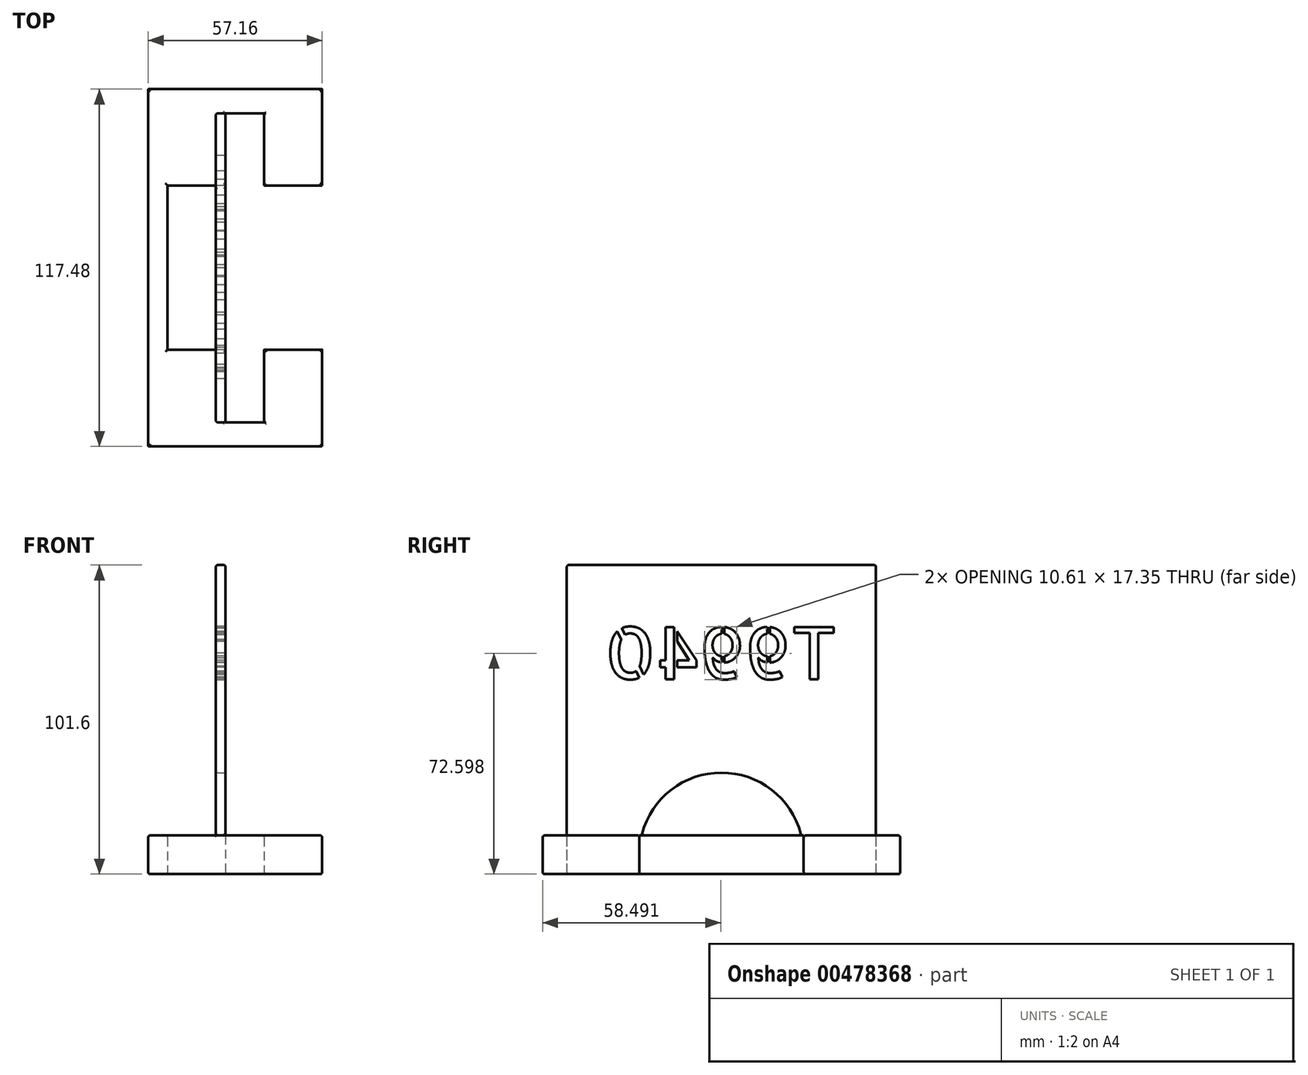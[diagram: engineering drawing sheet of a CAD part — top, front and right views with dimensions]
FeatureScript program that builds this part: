
annotation { "Feature Type Name" : "Feature", "Feature Type Description" : "" }
export const myFeature = defineFeature(function(context is Context, id is Id, definition is map)
    precondition{}
    {
        {
            var Q0;
            Q0=qCreatedBy(makeId("Top.planeOp"),FACE);
            var sketch = newSketch(context, id + "F0", { "sketchPlane" : qUnion([Q0])});
            skLineSegment(sketch, "E0.bottom", {"start": v(28.58, 58.74) * mm, "end": v(-28.57, 58.74) * mm});
            skLineSegment(sketch, "E0.top", {"start": v(28.58, -58.74) * mm, "end": v(-28.57, -58.74) * mm});
            skLineSegment(sketch, "E0.left", {"start": v(28.58, 58.74) * mm, "end": v(28.58, 27.05) * mm});
            skLineSegment(sketch, "E0.right", {"start": v(-28.57, 58.74) * mm, "end": v(-28.57, -58.74) * mm});
            skPoint(sketch, "E0.middle", {"position": v(0, 0) * mm});
            skLineSegment(sketch, "E1.bottom", {"start": v(9.53, 50.8) * mm, "end": v(-3.17, 50.8) * mm});
            skLineSegment(sketch, "E1.top", {"start": v(9.53, -50.8) * mm, "end": v(-3.17, -50.8) * mm});
            skLineSegment(sketch, "E1.left", {"start": v(9.53, 50.8) * mm, "end": v(9.53, 27.05) * mm});
            skLineSegment(sketch, "E1.right", {"start": v(-3.17, 50.8) * mm, "end": v(-3.17, 27.05) * mm});
            skLineSegment(sketch, "E2.bottom", {"start": v(28.58, -26.92) * mm, "end": v(9.53, -26.92) * mm});
            skLineSegment(sketch, "E2.top", {"start": v(28.58, 27.05) * mm, "end": v(9.53, 27.05) * mm});
            skLineSegment(sketch, "E2.right", {"start": v(-22.22, -26.92) * mm, "end": v(-22.22, 27.05) * mm});
            skPoint(sketch, "E2.middle", {"position": v(3.18, 0.06) * mm});
            skLineSegment(sketch, "E3.trimOffspring", {"start": v(28.58, -26.92) * mm, "end": v(28.58, -58.74) * mm});
            skLineSegment(sketch, "E4.trimOffspring", {"start": v(9.53, -26.92) * mm, "end": v(9.53, -50.8) * mm});
            skLineSegment(sketch, "E5.trimOffspring", {"start": v(-3.17, -26.92) * mm, "end": v(-3.17, -50.8) * mm});
            skLineSegment(sketch, "E6.trimOffspring", {"start": v(-3.17, 27.05) * mm, "end": v(-22.22, 27.05) * mm});
            skLineSegment(sketch, "E7.trimOffspring", {"start": v(-3.17, -26.92) * mm, "end": v(-22.22, -26.92) * mm});
            skSolve(sketch);
        }
        {
            var Q0;
            Q0 = qSketchRegion(id + "F0", true);
            extrude(context, id + "F1", {"entities" : qUnion([Q0]), "depth" : 12.7 * mm});
        }
        {
            var Q0;
            Q0=makeQuery(id+"F1.opExtrude","CAP_FACE",FACE,{"disambiguationData":[OSD([sQuery(id+"F0.wireOp",EDGE,"E0.bottom"),sQuery(id+"F0.wireOp",EDGE,"E0.top"),sQuery(id+"F0.wireOp",EDGE,"E0.left"),sQuery(id+"F0.wireOp",EDGE,"E0.right"),sQuery(id+"F0.wireOp",EDGE,"E1.bottom"),sQuery(id+"F0.wireOp",EDGE,"E1.top"),sQuery(id+"F0.wireOp",EDGE,"E1.left"),sQuery(id+"F0.wireOp",EDGE,"E1.right"),sQuery(id+"F0.wireOp",EDGE,"E2.bottom"),sQuery(id+"F0.wireOp",EDGE,"E2.top"),sQuery(id+"F0.wireOp",EDGE,"E2.right"),sQuery(id+"F0.wireOp",EDGE,"E3.trimOffspring"),sQuery(id+"F0.wireOp",EDGE,"E4.trimOffspring"),sQuery(id+"F0.wireOp",EDGE,"E5.trimOffspring"),sQuery(id+"F0.wireOp",EDGE,"E6.trimOffspring"),sQuery(id+"F0.wireOp",EDGE,"E7.trimOffspring")])],"isStart":false});
            var sketch = newSketch(context, id + "F2", { "sketchPlane" : qUnion([Q0])});
            skLineSegment(sketch, "E8.bottom", {"start": v(-3.17, 50.8) * mm, "end": v(-6.35, 50.8) * mm});
            skLineSegment(sketch, "E8.top", {"start": v(-3.17, -50.8) * mm, "end": v(-6.35, -50.8) * mm});
            skLineSegment(sketch, "E8.left", {"start": v(-3.17, 50.8) * mm, "end": v(-3.17, -50.8) * mm});
            skLineSegment(sketch, "E8.right", {"start": v(-6.35, 50.8) * mm, "end": v(-6.35, -50.8) * mm});
            skSolve(sketch);
        }
        {
            var Q0;
            Q0 = qSketchRegion(id + "F2", true);
            extrude(context, id + "F3", {"entities" : qUnion([Q0]), "operationType" : NewBodyOperationType.ADD, "depth" : 88.9 * mm});
        }
        {
            var Q0;
            Q0=makeQuery(id+"F3.boolean.opBoolean","MERGE",FACE,{"derivedFrom":[makeQuery(id+"F1.opExtrude","SWEPT_FACE",FACE,{"disambiguationData":[OSD([sQuery(id+"F0.wireOp",EDGE,"E1.right")])]}),makeQuery(id+"F1.opExtrude","SWEPT_FACE",FACE,{"disambiguationData":[OSD([sQuery(id+"F0.wireOp",EDGE,"E5.trimOffspring")])]}),makeQuery(id+"F3.opExtrude","SWEPT_FACE",FACE,{"disambiguationData":[OSD([sQuery(id+"F2.wireOp",EDGE,"E8.left")])]})]});
            var sketch = newSketch(context, id + "F4", { "sketchPlane" : qUnion([Q0])});
            skCircle(sketch, "E9", {"center": v(0, 6.35) * mm, "radius": 26.99 * mm});
            skSolve(sketch);
        }
        {
            var Q0;
            {var subQ0=sQuery(id+"F4.wireOp",EDGE,"E9");var subQ1=makeQuery(id+"F3.opExtrude","CAP_EDGE",EDGE,{"disambiguationData":[OSD([sQuery(id+"F2.wireOp",EDGE,"E8.left")])],"isStart":true});var subQ2=makeQuery(id+"F4.imprint","INTERSECT",VERTEX,{"disambiguationData":[OD(0.0)],"derivedFrom":[subQ1,subQ0]});Q0=makeQuery(id+"F4.imprint","IMPRINT",FACE,{"disambiguationData":[TD([[makeQuery(id+"F4.imprint","IMPRINT",EDGE,{"disambiguationData":[TD([[subQ2,-1.0]])],"derivedFrom":subQ0}),1.0]])]});}
            extrude(context, id + "F5", {"entities" : qUnion([Q0]), "operationType" : NewBodyOperationType.REMOVE, "oppositeDirection" : true, "depth" : 3.17 * mm});
        }
        {
            var Q0;
            Q0=makeQuery(id+"F3.opExtrude","CAP_FACE",FACE,{"disambiguationData":[OSD([sQuery(id+"F2.wireOp",EDGE,"E8.bottom"),sQuery(id+"F2.wireOp",EDGE,"E8.top"),sQuery(id+"F2.wireOp",EDGE,"E8.left"),sQuery(id+"F2.wireOp",EDGE,"E8.right")])],"isStart":false});
            fillet(context, id + "F6", {"entities" : qUnion([Q0]), "radius" : 0.64 * mm, "tangentPropagation" : true, "allowEdgeOverflow" : false});
        }
        {
            var Q0;
            Q0=makeQuery(id+"F3.opExtrude","SWEPT_EDGE",EDGE,{"disambiguationData":[OSD([sQuery(id+"F0.wireOp",EDGE,"E1.top"),sQuery(id+"F2.wireOp",EDGE,"E8.top"),sQuery(id+"F2.wireOp",EDGE,"E8.left")])]});
            var Q1;
            Q1=makeQuery(id+"F3.opExtrude","SWEPT_EDGE",EDGE,{"disambiguationData":[OSD([sQuery(id+"F0.wireOp",EDGE,"E1.bottom"),sQuery(id+"F2.wireOp",EDGE,"E8.bottom"),sQuery(id+"F2.wireOp",EDGE,"E8.left")])]});
            var Q2;
            Q2=makeQuery(id+"F3.opExtrude","SWEPT_EDGE",EDGE,{"disambiguationData":[OSD([sQuery(id+"F2.wireOp",EDGE,"E8.bottom"),sQuery(id+"F2.wireOp",EDGE,"E8.right")])]});
            var Q3;
            Q3=makeQuery(id+"F3.opExtrude","SWEPT_EDGE",EDGE,{"disambiguationData":[OSD([sQuery(id+"F2.wireOp",EDGE,"E8.top"),sQuery(id+"F2.wireOp",EDGE,"E8.right")])]});
            var Q4;
            Q4=makeQuery(id+"F1.opExtrude","CAP_EDGE",EDGE,{"disambiguationData":[OSD([sQuery(id+"F0.wireOp",EDGE,"E0.right")])],"isStart":false});
            var Q5;
            Q5=makeQuery(id+"F1.opExtrude","CAP_EDGE",EDGE,{"disambiguationData":[OSD([sQuery(id+"F0.wireOp",EDGE,"E0.top")])],"isStart":false});
            var Q6;
            Q6=makeQuery(id+"F1.opExtrude","CAP_EDGE",EDGE,{"disambiguationData":[OSD([sQuery(id+"F0.wireOp",EDGE,"E0.bottom")])],"isStart":false});
            var Q7;
            Q7=makeQuery(id+"F1.opExtrude","CAP_EDGE",EDGE,{"disambiguationData":[OSD([sQuery(id+"F0.wireOp",EDGE,"E3.trimOffspring")])],"isStart":false});
            var Q8;
            Q8=makeQuery(id+"F1.opExtrude","CAP_EDGE",EDGE,{"disambiguationData":[OSD([sQuery(id+"F0.wireOp",EDGE,"E2.bottom")])],"isStart":false});
            var Q9;
            Q9=makeQuery(id+"F1.opExtrude","CAP_EDGE",EDGE,{"disambiguationData":[OSD([sQuery(id+"F0.wireOp",EDGE,"E2.top")])],"isStart":false});
            var Q10;
            Q10=makeQuery(id+"F1.opExtrude","CAP_EDGE",EDGE,{"disambiguationData":[OSD([sQuery(id+"F0.wireOp",EDGE,"E0.left")])],"isStart":false});
            var Q11;
            Q11=makeQuery(id+"F1.opExtrude","CAP_EDGE",EDGE,{"disambiguationData":[OSD([sQuery(id+"F0.wireOp",EDGE,"E2.right")])],"isStart":false});
            var Q12;
            {var subQ0=sQuery(id+"F0.wireOp",EDGE,"E6.trimOffspring");Q12=makeQuery(id+"F3.boolean.opBoolean","SPLIT",EDGE,{"disambiguationData":[topologyDisambiguationEdgeConnected([makeQuery(id+"F1.opExtrude","CAP_FACE",FACE,{"disambiguationData":[OSD([sQuery(id+"F0.wireOp",EDGE,"E0.bottom"),sQuery(id+"F0.wireOp",EDGE,"E0.top"),sQuery(id+"F0.wireOp",EDGE,"E0.left"),sQuery(id+"F0.wireOp",EDGE,"E0.right"),sQuery(id+"F0.wireOp",EDGE,"E1.bottom"),sQuery(id+"F0.wireOp",EDGE,"E1.top"),sQuery(id+"F0.wireOp",EDGE,"E1.left"),sQuery(id+"F0.wireOp",EDGE,"E1.right"),sQuery(id+"F0.wireOp",EDGE,"E2.bottom"),sQuery(id+"F0.wireOp",EDGE,"E2.top"),sQuery(id+"F0.wireOp",EDGE,"E2.right"),sQuery(id+"F0.wireOp",EDGE,"E3.trimOffspring"),sQuery(id+"F0.wireOp",EDGE,"E4.trimOffspring"),sQuery(id+"F0.wireOp",EDGE,"E5.trimOffspring"),subQ0,sQuery(id+"F0.wireOp",EDGE,"E7.trimOffspring")])],"isStart":false})])],"derivedFrom":makeQuery(id+"F1.opExtrude","CAP_EDGE",EDGE,{"disambiguationData":[OSD([subQ0])],"isStart":false})});}
            var Q13;
            {var subQ0=sQuery(id+"F0.wireOp",EDGE,"E7.trimOffspring");Q13=makeQuery(id+"F3.boolean.opBoolean","SPLIT",EDGE,{"disambiguationData":[topologyDisambiguationEdgeConnected([makeQuery(id+"F1.opExtrude","CAP_FACE",FACE,{"disambiguationData":[OSD([sQuery(id+"F0.wireOp",EDGE,"E0.bottom"),sQuery(id+"F0.wireOp",EDGE,"E0.top"),sQuery(id+"F0.wireOp",EDGE,"E0.left"),sQuery(id+"F0.wireOp",EDGE,"E0.right"),sQuery(id+"F0.wireOp",EDGE,"E1.bottom"),sQuery(id+"F0.wireOp",EDGE,"E1.top"),sQuery(id+"F0.wireOp",EDGE,"E1.left"),sQuery(id+"F0.wireOp",EDGE,"E1.right"),sQuery(id+"F0.wireOp",EDGE,"E2.bottom"),sQuery(id+"F0.wireOp",EDGE,"E2.top"),sQuery(id+"F0.wireOp",EDGE,"E2.right"),sQuery(id+"F0.wireOp",EDGE,"E3.trimOffspring"),sQuery(id+"F0.wireOp",EDGE,"E4.trimOffspring"),sQuery(id+"F0.wireOp",EDGE,"E5.trimOffspring"),sQuery(id+"F0.wireOp",EDGE,"E6.trimOffspring"),subQ0])],"isStart":false})])],"derivedFrom":makeQuery(id+"F1.opExtrude","CAP_EDGE",EDGE,{"disambiguationData":[OSD([subQ0])],"isStart":false})});}
            var Q14;
            Q14=makeQuery(id+"F5.boolean.opBoolean","COPY",EDGE,{"derivedFrom":makeQuery(id+"F5.opExtrude","CAP_EDGE",EDGE,{"disambiguationData":[OSD([sQuery(id+"F4.wireOp",EDGE,"E9")])],"isStart":true})});
            var Q15;
            Q15=makeQuery(id+"F5.boolean.opBoolean","COPY",EDGE,{"derivedFrom":makeQuery(id+"F5.opExtrude","CAP_EDGE",EDGE,{"disambiguationData":[OSD([sQuery(id+"F4.wireOp",EDGE,"E9")])],"isStart":false})});
            var Q16;
            {var subQ0=sQuery(id+"F4.wireOp",EDGE,"E9");var subQ1=sQuery(id+"F2.wireOp",EDGE,"E8.left");Q16=makeQuery(id+"F5.boolean.opBoolean","COPY",EDGE,{"derivedFrom":makeQuery(id+"F5.opExtrude","SWEPT_EDGE",EDGE,{"disambiguationData":[OSD([subQ1,subQ0]),TDD([makeQuery(id+"F4.imprint","INTERSECT",VERTEX,{"disambiguationData":[OD(0.0)],"derivedFrom":[makeQuery(id+"F3.opExtrude","CAP_EDGE",EDGE,{"disambiguationData":[OSD([subQ1])],"isStart":true}),subQ0]})])]})});}
            var Q17;
            Q17=makeQuery(id+"F5.boolean.opBoolean","COPY",FACE,{"derivedFrom":makeQuery(id+"F5.opExtrude","SWEPT_FACE",FACE,{"disambiguationData":[OSD([sQuery(id+"F4.wireOp",EDGE,"E9")])]})});
            var Q18;
            Q18=makeQuery(id+"F1.opExtrude","CAP_EDGE",EDGE,{"disambiguationData":[OSD([sQuery(id+"F0.wireOp",EDGE,"E4.trimOffspring")])],"isStart":false});
            var Q19;
            Q19=makeQuery(id+"F1.opExtrude","CAP_EDGE",EDGE,{"disambiguationData":[OSD([sQuery(id+"F0.wireOp",EDGE,"E1.left")])],"isStart":false});
            var Q20;
            Q20=makeQuery(id+"F1.opExtrude","CAP_FACE",FACE,{"disambiguationData":[OSD([sQuery(id+"F0.wireOp",EDGE,"E0.bottom"),sQuery(id+"F0.wireOp",EDGE,"E0.top"),sQuery(id+"F0.wireOp",EDGE,"E0.left"),sQuery(id+"F0.wireOp",EDGE,"E0.right"),sQuery(id+"F0.wireOp",EDGE,"E1.bottom"),sQuery(id+"F0.wireOp",EDGE,"E1.top"),sQuery(id+"F0.wireOp",EDGE,"E1.left"),sQuery(id+"F0.wireOp",EDGE,"E1.right"),sQuery(id+"F0.wireOp",EDGE,"E2.bottom"),sQuery(id+"F0.wireOp",EDGE,"E2.top"),sQuery(id+"F0.wireOp",EDGE,"E2.right"),sQuery(id+"F0.wireOp",EDGE,"E3.trimOffspring"),sQuery(id+"F0.wireOp",EDGE,"E4.trimOffspring"),sQuery(id+"F0.wireOp",EDGE,"E5.trimOffspring"),sQuery(id+"F0.wireOp",EDGE,"E6.trimOffspring"),sQuery(id+"F0.wireOp",EDGE,"E7.trimOffspring")])],"isStart":true});
            fillet(context, id + "F7", {"entities" : qUnion([Q0, Q1, Q2, Q3, Q4, Q5, Q6, Q7, Q8, Q9, Q10, Q11, Q12, Q13, Q14, Q15, Q16, Q17, Q18, Q19, Q20]), "radius" : 0.64 * mm, "tangentPropagation" : true, "allowEdgeOverflow" : false});
        }
        {
            var Q0;
            Q0=makeQuery(id+"F3.opExtrude","SWEPT_FACE",FACE,{"disambiguationData":[OSD([sQuery(id+"F2.wireOp",EDGE,"E8.right")])]});
            var sketch = newSketch(context, id + "F8", { "sketchPlane" : qUnion([Q0])});
            skText(sketch, "E10", { "text": "T9940", "fontName": "AllertaStencil-Regular.ttf"});
            const initialGuessF8  = {"E10": [-0.0381, 0.06404, 1, 0, 0.01712]};
            skSetInitialGuess(sketch, initialGuessF8);
            skSolve(sketch);
        }
        {
            var Q0;
            Q0 = qSketchRegion(id + "F8", true);
            extrude(context, id + "F9", {"entities" : qUnion([Q0]), "operationType" : NewBodyOperationType.REMOVE, "oppositeDirection" : true, "depth" : 6.35 * mm});
        }
    });
